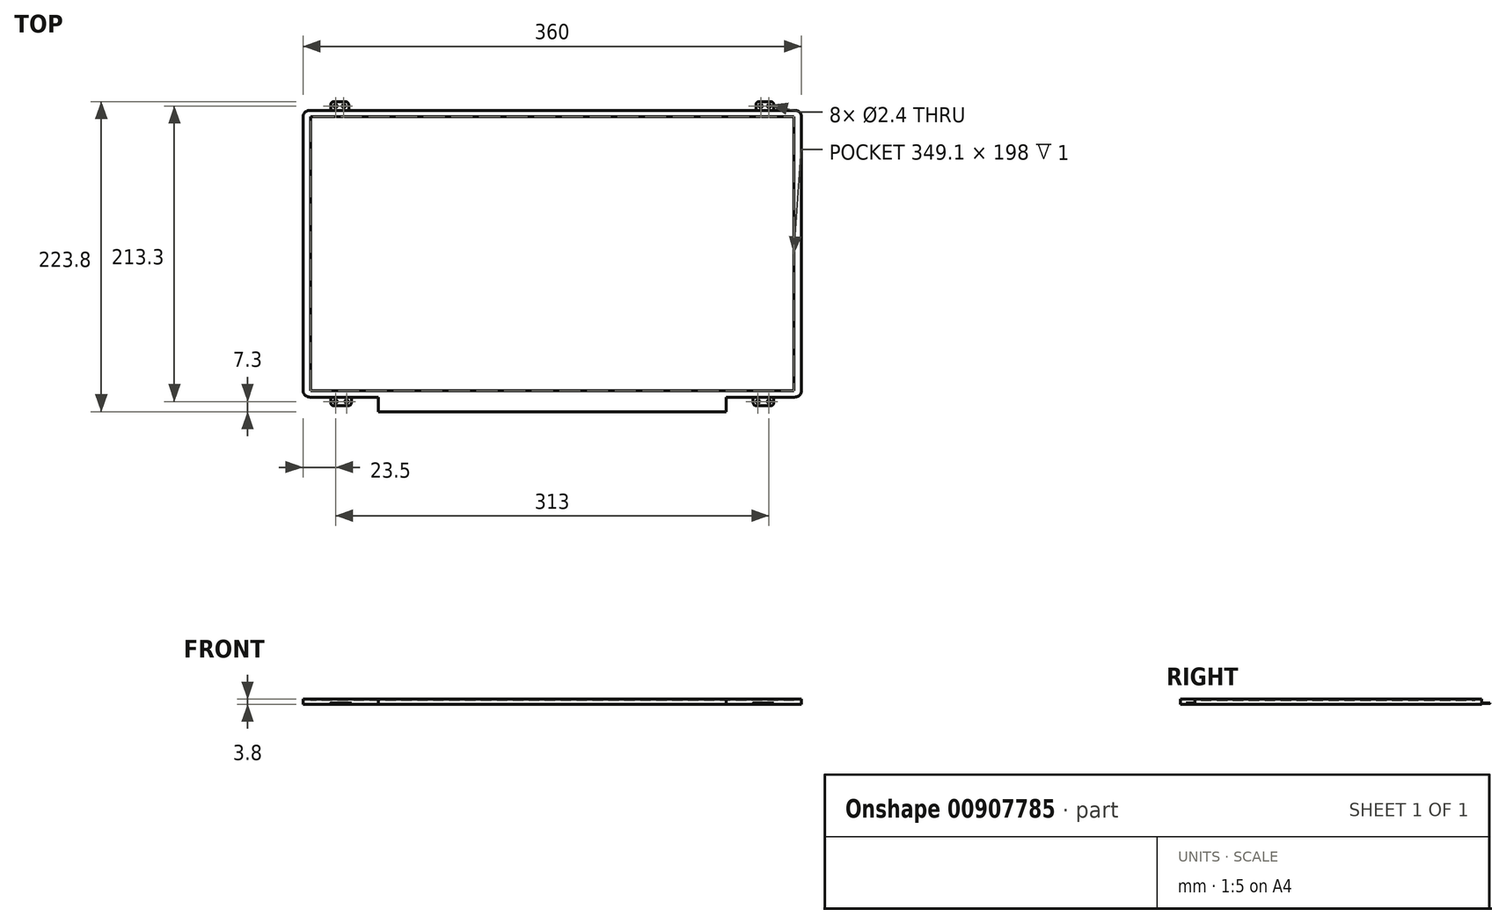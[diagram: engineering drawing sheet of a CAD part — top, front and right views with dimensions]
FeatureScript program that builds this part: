
annotation { "Feature Type Name" : "Feature", "Feature Type Description" : "" }
export const myFeature = defineFeature(function(context is Context, id is Id, definition is map)
    precondition{}
    {
        {
            var Q0;
            Q0=qCreatedBy(makeId("Top.planeOp"),FACE);
            var sketch = newSketch(context, id + "F0", { "sketchPlane" : qUnion([Q0])});
            skLineSegment(sketch, "E0.bottom", {"start": v(180, -103.5) * mm, "end": v(-180, -103.5) * mm});
            skLineSegment(sketch, "E0.top", {"start": v(180, 103.5) * mm, "end": v(-180, 103.5) * mm});
            skLineSegment(sketch, "E0.left", {"start": v(180, -103.5) * mm, "end": v(180, 103.5) * mm});
            skLineSegment(sketch, "E0.right", {"start": v(-180, -103.5) * mm, "end": v(-180, 103.5) * mm});
            skPoint(sketch, "E0.middle", {"position": v(0, 0) * mm});
            skSolve(sketch);
        }
        {
            var Q0;
            Q0 = qSketchRegion(id + "F0", true);
            extrude(context, id + "F1", {"entities" : qUnion([Q0]), "depth" : 3.8 * mm, "offsetDistance" : 25 * mm});
        }
        {
            var Q0;
            Q0=makeQuery(id+"F1.opExtrude","SWEPT_EDGE",EDGE,{"disambiguationData":[OSD([sQuery(id+"F0.wireOp",EDGE,"E0.top"),sQuery(id+"F0.wireOp",EDGE,"E0.left")])]});
            var Q1;
            Q1=makeQuery(id+"F1.opExtrude","SWEPT_EDGE",EDGE,{"disambiguationData":[OSD([sQuery(id+"F0.wireOp",EDGE,"E0.top"),sQuery(id+"F0.wireOp",EDGE,"E0.right")])]});
            var Q2;
            Q2=makeQuery(id+"F1.opExtrude","SWEPT_EDGE",EDGE,{"disambiguationData":[OSD([sQuery(id+"F0.wireOp",EDGE,"E0.bottom"),sQuery(id+"F0.wireOp",EDGE,"E0.right")])]});
            var Q3;
            Q3=makeQuery(id+"F1.opExtrude","SWEPT_EDGE",EDGE,{"disambiguationData":[OSD([sQuery(id+"F0.wireOp",EDGE,"E0.bottom"),sQuery(id+"F0.wireOp",EDGE,"E0.left")])]});
            fillet(context, id + "F2", {"entities" : qUnion([Q0, Q1, Q2, Q3]), "radius" : 5 * mm, "tangentPropagation" : true, "allowEdgeOverflow" : false});
        }
        {
            var Q0;
            Q0=makeQuery(id+"F1.opExtrude","CAP_FACE",FACE,{"disambiguationData":[OSD([sQuery(id+"F0.wireOp",EDGE,"E0.bottom"),sQuery(id+"F0.wireOp",EDGE,"E0.top"),sQuery(id+"F0.wireOp",EDGE,"E0.left"),sQuery(id+"F0.wireOp",EDGE,"E0.right")])],"isStart":false});
            var sketch = newSketch(context, id + "F3", { "sketchPlane" : qUnion([Q0])});
            skLineSegment(sketch, "E1.bottom", {"start": v(174.55, -99) * mm, "end": v(-174.55, -99) * mm});
            skLineSegment(sketch, "E1.top", {"start": v(174.55, 99) * mm, "end": v(-174.55, 99) * mm});
            skLineSegment(sketch, "E1.left", {"start": v(174.55, -99) * mm, "end": v(174.55, 99) * mm});
            skLineSegment(sketch, "E1.right", {"start": v(-174.55, -119.3) * mm, "end": v(-174.55, 99) * mm});
            skPoint(sketch, "E1.middle", {"position": v(0, 0) * mm});
            skSolve(sketch);
        }
        {
            var Q0;
            Q0 = qSketchRegion(id + "F3", true);
            extrude(context, id + "F4", {"entities" : qUnion([Q0]), "operationType" : NewBodyOperationType.REMOVE, "oppositeDirection" : true, "depth" : 1 * mm, "offsetDistance" : 25 * mm});
        }
        {
            var Q0;
            Q0=qCreatedBy(makeId("Top.planeOp"),FACE);
            cPlane(context, id + "F5", {"entities" : qUnion([Q0]), "cplaneType" : CPlaneType.OFFSET, "offset" : 0.8 * mm, "width" : 150 * mm, "height" : 150 * mm});
        }
        {
            var Q0;
            Q0=qCreatedBy(id+"F5.planeOp",FACE);
            var sketch = newSketch(context, id + "F6", { "sketchPlane" : qUnion([Q0])});
            skLineSegment(sketch, "E2.bottom", {"start": v(-147, 109.8) * mm, "end": v(-160, 109.8) * mm});
            skLineSegment(sketch, "E2.top", {"start": v(-147, 103.5) * mm, "end": v(-160, 103.5) * mm});
            skLineSegment(sketch, "E2.left", {"start": v(-147, 109.8) * mm, "end": v(-147, 103.5) * mm});
            skLineSegment(sketch, "E2.right", {"start": v(-160, 109.8) * mm, "end": v(-160, 103.5) * mm});
            skPoint(sketch, "E2.middle", {"position": v(-153.5, 106.65) * mm});
            skLineSegment(sketch, "E3.bottom", {"start": v(160, 103.5) * mm, "end": v(147, 103.5) * mm});
            skLineSegment(sketch, "E3.top", {"start": v(160, 109.8) * mm, "end": v(147, 109.8) * mm});
            skLineSegment(sketch, "E3.left", {"start": v(160, 103.5) * mm, "end": v(160, 109.8) * mm});
            skLineSegment(sketch, "E3.right", {"start": v(147, 103.5) * mm, "end": v(147, 109.8) * mm});
            skLineSegment(sketch, "E4.bottom", {"start": v(-160, -103.5) * mm, "end": v(-145, -103.5) * mm});
            skLineSegment(sketch, "E4.top", {"start": v(-160, -109.8) * mm, "end": v(-145, -109.8) * mm});
            skLineSegment(sketch, "E4.left", {"start": v(-160, -103.5) * mm, "end": v(-160, -109.8) * mm});
            skLineSegment(sketch, "E4.right", {"start": v(-145, -103.5) * mm, "end": v(-145, -109.8) * mm});
            skLineSegment(sketch, "E5.bottom", {"start": v(160, -103.5) * mm, "end": v(145, -103.5) * mm});
            skLineSegment(sketch, "E5.top", {"start": v(160, -109.8) * mm, "end": v(145, -109.8) * mm});
            skLineSegment(sketch, "E5.left", {"start": v(160, -103.5) * mm, "end": v(160, -109.8) * mm});
            skLineSegment(sketch, "E5.right", {"start": v(145, -103.5) * mm, "end": v(145, -109.8) * mm});
            skSolve(sketch);
        }
        {
            var Q0;
            Q0 = qSketchRegion(id + "F6", true);
            extrude(context, id + "F7", {"entities" : qUnion([Q0]), "operationType" : NewBodyOperationType.ADD, "depth" : 0.3 * mm, "offsetDistance" : 25 * mm});
        }
        {
            var Q0;
            Q0=makeQuery(id+"F7.opExtrude","SWEPT_EDGE",EDGE,{"disambiguationData":[OSD([sQuery(id+"F6.wireOp",EDGE,"E2.bottom"),sQuery(id+"F6.wireOp",EDGE,"E2.right")])]});
            var Q1;
            Q1=makeQuery(id+"F7.opExtrude","SWEPT_EDGE",EDGE,{"disambiguationData":[OSD([sQuery(id+"F6.wireOp",EDGE,"E2.bottom"),sQuery(id+"F6.wireOp",EDGE,"E2.left")])]});
            var Q2;
            Q2=makeQuery(id+"F7.opExtrude","SWEPT_EDGE",EDGE,{"disambiguationData":[OSD([sQuery(id+"F6.wireOp",EDGE,"E3.top"),sQuery(id+"F6.wireOp",EDGE,"E3.right")])]});
            var Q3;
            Q3=makeQuery(id+"F7.opExtrude","SWEPT_EDGE",EDGE,{"disambiguationData":[OSD([sQuery(id+"F6.wireOp",EDGE,"E3.top"),sQuery(id+"F6.wireOp",EDGE,"E3.left")])]});
            var Q4;
            Q4=makeQuery(id+"F7.opExtrude","SWEPT_EDGE",EDGE,{"disambiguationData":[OSD([sQuery(id+"F6.wireOp",EDGE,"E5.top"),sQuery(id+"F6.wireOp",EDGE,"E5.right")])]});
            var Q5;
            Q5=makeQuery(id+"F7.opExtrude","SWEPT_EDGE",EDGE,{"disambiguationData":[OSD([sQuery(id+"F6.wireOp",EDGE,"E5.top"),sQuery(id+"F6.wireOp",EDGE,"E5.left")])]});
            var Q6;
            Q6=makeQuery(id+"F7.opExtrude","SWEPT_EDGE",EDGE,{"disambiguationData":[OSD([sQuery(id+"F6.wireOp",EDGE,"E4.top"),sQuery(id+"F6.wireOp",EDGE,"E4.left")])]});
            var Q7;
            Q7=makeQuery(id+"F7.opExtrude","SWEPT_EDGE",EDGE,{"disambiguationData":[OSD([sQuery(id+"F6.wireOp",EDGE,"E4.top"),sQuery(id+"F6.wireOp",EDGE,"E4.right")])]});
            fillet(context, id + "F8", {"entities" : qUnion([Q0, Q1, Q2, Q3, Q4, Q5, Q6, Q7]), "radius" : 2.4 * mm, "tangentPropagation" : true, "allowEdgeOverflow" : false});
        }
        {
            var Q0;
            Q0=makeQuery(id+"F7.opExtrude","CAP_FACE",FACE,{"disambiguationData":[OSD([sQuery(id+"F6.wireOp",EDGE,"E2.bottom"),sQuery(id+"F6.wireOp",EDGE,"E2.top"),sQuery(id+"F6.wireOp",EDGE,"E2.left"),sQuery(id+"F6.wireOp",EDGE,"E2.right")])],"isStart":false});
            var sketch = newSketch(context, id + "F9", { "sketchPlane" : qUnion([Q0])});
            skCircle(sketch, "E6", {"center": v(-156.5, 106.6) * mm, "radius": 1.2 * mm});
            skCircle(sketch, "E7", {"center": v(-150.5, 106.6) * mm, "radius": 1.2 * mm});
            skCircle(sketch, "E8", {"center": v(150.5, 106.6) * mm, "radius": 1.2 * mm});
            skCircle(sketch, "E9", {"center": v(156.5, 106.6) * mm, "radius": 1.2 * mm});
            skCircle(sketch, "E10", {"center": v(148.5, -106.7) * mm, "radius": 1.2 * mm});
            skCircle(sketch, "E11", {"center": v(156.5, -106.7) * mm, "radius": 1.2 * mm});
            skCircle(sketch, "E12", {"center": v(-156.5, -106.7) * mm, "radius": 1.2 * mm});
            skCircle(sketch, "E13", {"center": v(-148.5, -106.7) * mm, "radius": 1.2 * mm});
            skSolve(sketch);
        }
        {
            var Q0;
            Q0 = qSketchRegion(id + "F9", true);
            extrude(context, id + "F10", {"entities" : qUnion([Q0]), "operationType" : NewBodyOperationType.REMOVE, "endBound" : BoundingType.THROUGH_ALL, "oppositeDirection" : true, "depth" : 25 * mm, "offsetDistance" : 25 * mm});
        }
        {
            var Q0;
            Q0=qCreatedBy(makeId("Top.planeOp"),FACE);
            var sketch = newSketch(context, id + "F11", { "sketchPlane" : qUnion([Q0])});
            skLineSegment(sketch, "E14.bottom", {"start": v(125.5, -114) * mm, "end": v(-125.5, -114) * mm});
            skLineSegment(sketch, "E14.top", {"start": v(125.5, -103.5) * mm, "end": v(-125.5, -103.5) * mm});
            skLineSegment(sketch, "E14.left", {"start": v(125.5, -114) * mm, "end": v(125.5, -103.5) * mm});
            skLineSegment(sketch, "E14.right", {"start": v(-125.5, -114) * mm, "end": v(-125.5, -103.5) * mm});
            skPoint(sketch, "E14.middle", {"position": v(0, -108.75) * mm});
            skSolve(sketch);
        }
        {
            var Q0;
            Q0 = qSketchRegion(id + "F11", true);
            extrude(context, id + "F12", {"entities" : qUnion([Q0]), "operationType" : NewBodyOperationType.ADD, "depth" : 3.8 * mm, "offsetDistance" : 25 * mm});
        }
    });
